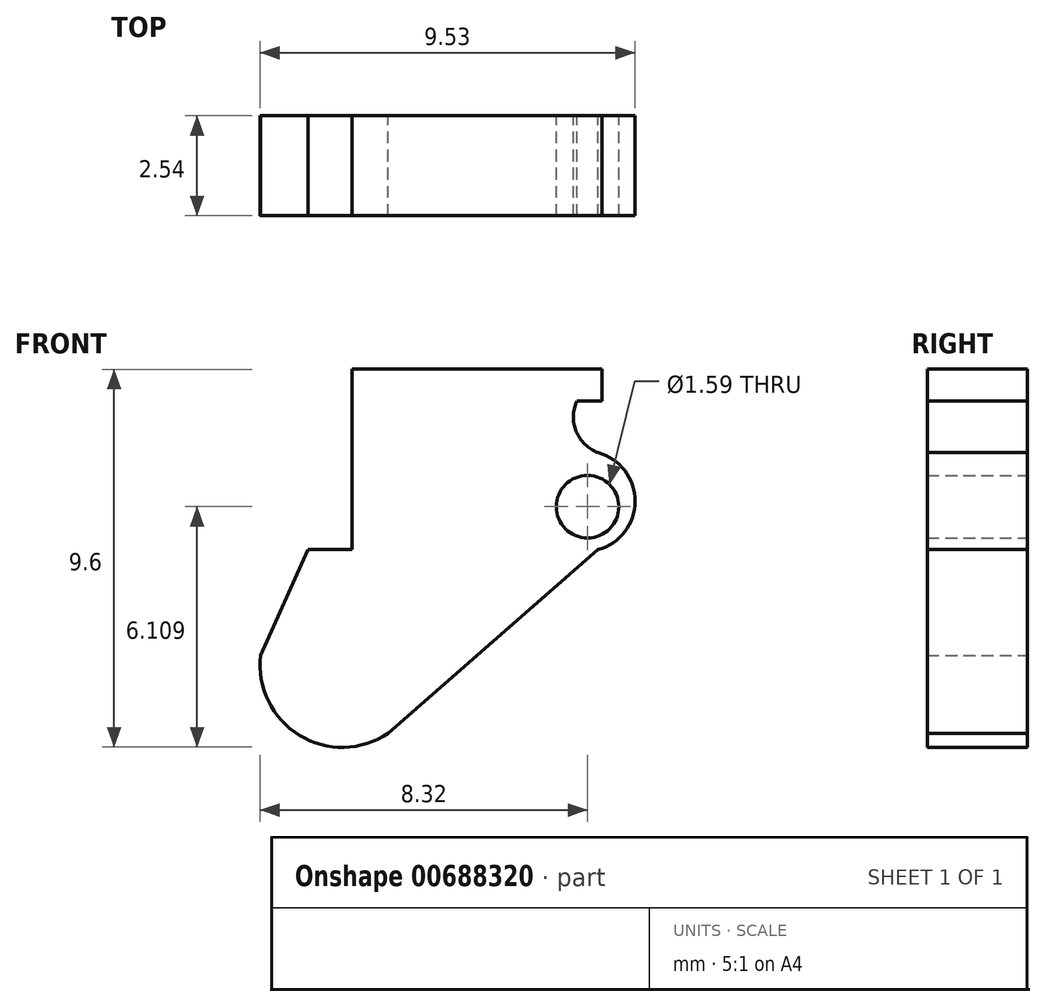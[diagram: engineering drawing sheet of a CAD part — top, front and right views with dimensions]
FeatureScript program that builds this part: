
annotation { "Feature Type Name" : "Feature", "Feature Type Description" : "" }
export const myFeature = defineFeature(function(context is Context, id is Id, definition is map)
    precondition{}
    {
        {
            var Q0;
            Q0=qCreatedBy(makeId("Front.planeOp"),FACE);
            var sketch = newSketch(context, id + "F0", { "sketchPlane" : qUnion([Q0])});
            skLineSegment(sketch, "E0", {"start": v(-50.18, 56.82) * mm, "end": v(-42.81, 56.82) * mm});
            skLineSegment(sketch, "E1", {"start": v(-43.35, 60.6) * mm, "end": v(-42.7, 60.6) * mm});
            skLineSegment(sketch, "E2", {"start": v(-42.7, 60.6) * mm, "end": v(-42.7, 61.4) * mm});
            skLineSegment(sketch, "E3", {"start": v(-42.7, 61.4) * mm, "end": v(-49.06, 61.4) * mm});
            skPoint(sketch, "E4.positionSnap0", {"position": v(-42.81, 56.82) * mm});
            skArc(sketch, "E5", {"start": v(-42.81, 56.82) * mm, "mid": v(-41.87, 58.05) * mm, "end": v(-42.81, 59.28) * mm});
            skArc(sketch, "E6", {"start": v(-43.35, 60.6) * mm, "mid": v(-43.37, 59.82) * mm, "end": v(-42.81, 59.28) * mm});
            skPoint(sketch, "E7", {"position": v(-43.08, 57.9) * mm});
            skLineSegment(sketch, "E8", {"start": v(-42.81, 56.82) * mm, "end": v(-48.15, 52.15) * mm});
            skLineSegment(sketch, "E9", {"start": v(-50.18, 56.82) * mm, "end": v(-51.39, 54.13) * mm});
            skArc(sketch, "E10", {"start": v(-51.39, 54.13) * mm, "mid": v(-50.4, 52.1) * mm, "end": v(-48.15, 52.15) * mm});
            skLineSegment(sketch, "E11", {"start": v(-49.06, 61.4) * mm, "end": v(-49.06, 56.82) * mm});
            skLineSegment(sketch, "E12", {"start": v(-49.06, 56.82) * mm, "end": v(-50.18, 56.82) * mm});
            skSolve(sketch);
        }
        {
            var Q0;
            Q0=makeQuery(id+"F0.imprint","IMPRINT",FACE,{"disambiguationData":[TD([[makeQuery(id+"F0.imprint","IMPRINT",EDGE,{"derivedFrom":sQuery(id+"F0.wireOp",EDGE,"E0")}),1.0]])]});
            var Q1;
            Q1=makeQuery(id+"F0.imprint","IMPRINT",FACE,{"disambiguationData":[TD([[makeQuery(id+"F0.imprint","IMPRINT",EDGE,{"derivedFrom":sQuery(id+"F0.wireOp",EDGE,"xP9mZdZE-mmRF-9zId-akvi-YD02wX0ZP1x8")}),-1.0]])]});
            var Q2;
            Q2=makeQuery(id+"F0.imprint","IMPRINT",FACE,{"disambiguationData":[TD([[makeQuery(id+"F0.imprint","IMPRINT",EDGE,{"derivedFrom":sQuery(id+"F0.wireOp",EDGE,"E0")}),-1.0]])]});
            extrude(context, id + "F1", {"entities" : qUnion([Q0, Q1, Q2]), "depth" : 2.54 * mm, "offsetDistance" : 25.4 * mm});
        }
        {
            var Q0;
            Q0=sQuery(id+"F0.wireOp",VERTEX,"E4");
            var Q1;
            Q1=sQuery(id+"F0.wireOp",VERTEX,"E7");
            var Q2;
            Q2=makeQuery(id+"F1.opExtrude","SWEPT_BODY",BODY,{"disambiguationData":[OSD([sQuery(id+"F0.wireOp",EDGE,"E0"),sQuery(id+"F0.wireOp",EDGE,"E1"),sQuery(id+"F0.wireOp",EDGE,"E2"),sQuery(id+"F0.wireOp",EDGE,"E3"),sQuery(id+"F0.wireOp",EDGE,"APpErOPz-oVv4-zX3a-hdGy-sYNYCfcGIScF"),sQuery(id+"F0.wireOp",EDGE,"SFqtDq2M-Xetr-kTGk-NAG9-2QiyaFxS5P29"),sQuery(id+"F0.wireOp",EDGE,"mu96lxOS-Pbau-Vrwh-ehJZ-DVPgRLEnjYBN"),sQuery(id+"F0.wireOp",EDGE,"oYmiaQOi-sj9O-S32n-V6Et-LtSNtxMS9J1O"),sQuery(id+"F0.wireOp",EDGE,"6duRIBZr-XkHb-Bjo9-nLKe-GiQfL7BW4F7T")])]});
            hole(context, id + "F2", {"style" : HoleStyle.SIMPLE, "endStyle" : HoleEndStyle.THROUGH, "oppositeDirection" : true, "holeDiameter" : 1.59 * mm, "majorDiameter" : 6.35 * mm, "isTappedThrough" : true, "tappedDepth" : 12.7 * mm, "tapClearance" : 3, "locations" : qUnion([Q0, Q1]), "scope" : qUnion([Q2])});
        }
    });
